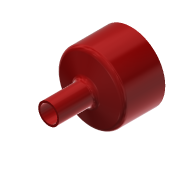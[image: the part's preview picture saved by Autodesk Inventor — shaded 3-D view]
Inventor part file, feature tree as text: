
AUTODESK INVENTOR PART (.ipt)
format: ipt  version: 2019.4 (Build 234330000, 330)  size: 172,544 bytes
history: native  units: mm
features: reference x4, other x4, sketch x3, extrude x2, revolve x1, fillet x1, projected_geometry x1
ambient origin geometry x8: Origin, YZ Plane, XZ Plane, XY Plane, X Axis, Y Axis, Z Axis, Center Point
bodies: Solid1 (feature_tree)
feature tree (16):
  revolve  "Revolution1"  [1 undecoded]
  extrude  "Extrusion2"  Depth=13.0mm
  extrude  "Extrusion3"  Depth=2.0mm
  fillet  "Fillet2"  Radius=5.0mm
  sketch  "Sketch1"  dims[d6=90.0deg d12=4.0mm]
  reference  "Reference1"
  sketch  "Sketch4"  dims[d13=0.0mm d15=13.0mm]
  reference  "Reference2"
  projected_geometry  "Projected Loop2"
  sketch  "Sketch5"  dims[d16=0.0mm d17=2.0mm d19=5.0mm d20=14.0mm d21=6.5mm d22=15.0mm d23=0.0mm d24=2.0mm d26=12.0mm d27=-0.523599mm d28=0.2mm]
  reference  "Reference3"
  reference  "Reference4"
  other  "Assemlby_OpenOxygen.iam"
  other  "00_Sensirion_Flowsensor:1"
  other  "01_Connector_T:1"
  other  "03_OpenOxygen_Box:1"
note: 1 required parameter value undecoded (feature->parameter linkage not recoverable at this tier; creation-order binding heuristic only, values carry confidence <= 0.55)
